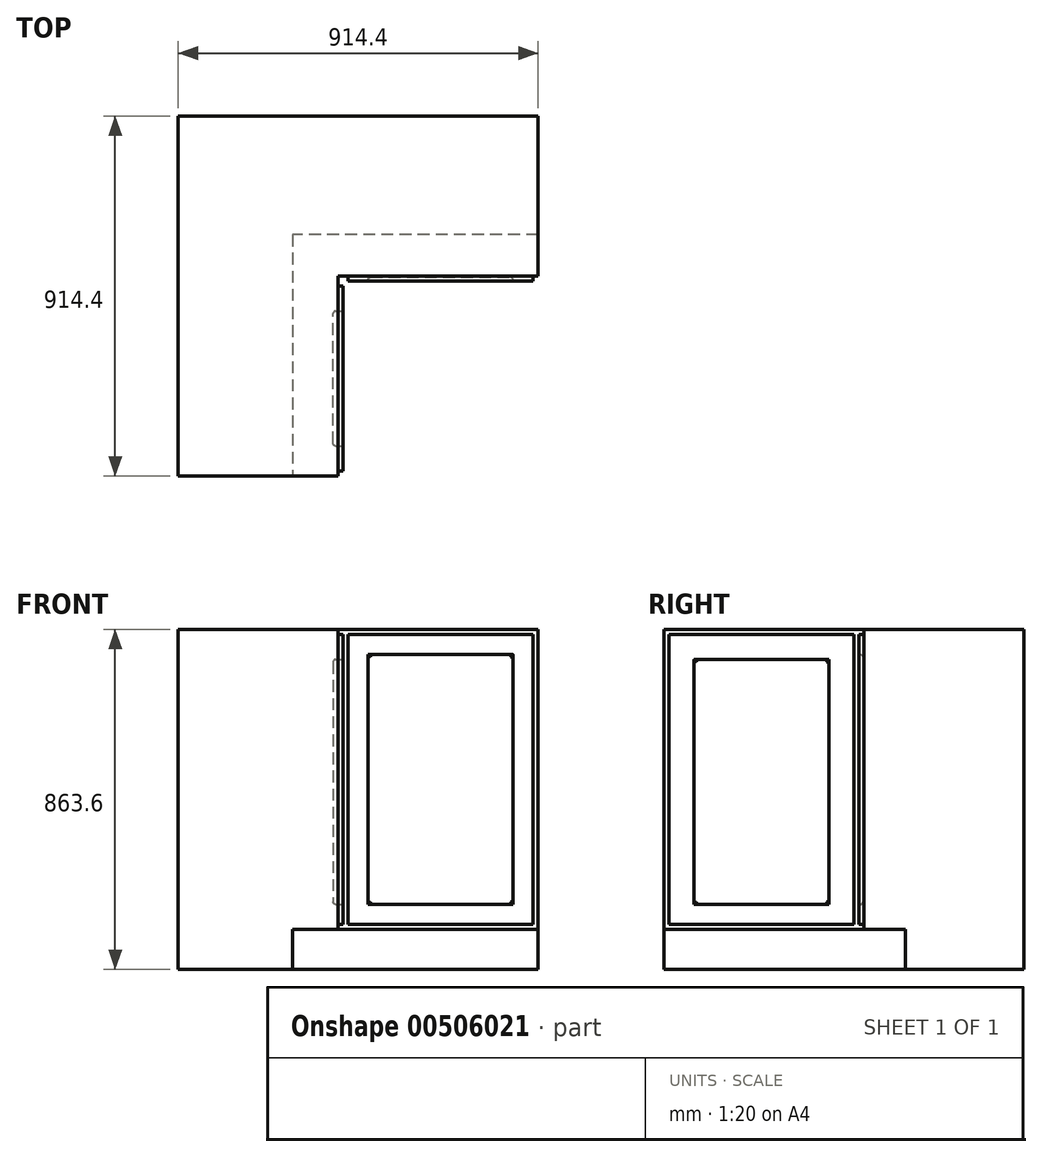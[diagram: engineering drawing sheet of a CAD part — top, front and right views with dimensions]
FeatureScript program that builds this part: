
annotation { "Feature Type Name" : "Feature", "Feature Type Description" : "" }
export const myFeature = defineFeature(function(context is Context, id is Id, definition is map)
    precondition{}
    {
        {
            var Q0;
            Q0=qCreatedBy(makeId("Top.planeOp"),FACE);
            var sketch = newSketch(context, id + "F0", { "sketchPlane" : qUnion([Q0])});
            skLineSegment(sketch, "E0", {"start": v(0, 0) * mm, "end": v(0, 914.4) * mm});
            skLineSegment(sketch, "E1", {"start": v(0, 914.4) * mm, "end": v(914.4, 914.4) * mm});
            skLineSegment(sketch, "E2", {"start": v(914.4, 914.4) * mm, "end": v(914.4, 495.3) * mm});
            skLineSegment(sketch, "E3", {"start": v(914.4, 495.3) * mm, "end": v(419.1, 495.3) * mm});
            skLineSegment(sketch, "E4", {"start": v(419.1, 495.3) * mm, "end": v(419.1, 0) * mm});
            skLineSegment(sketch, "E5", {"start": v(419.1, 0) * mm, "end": v(0, 0) * mm});
            skSolve(sketch);
        }
        {
            var Q0;
            Q0=makeQuery(id+"F0.imprint","IMPRINT",FACE,{"disambiguationData":[TD([[makeQuery(id+"F0.imprint","IMPRINT",EDGE,{"derivedFrom":sQuery(id+"F0.wireOp",EDGE,"E0")}),-1.0]])]});
            extrude(context, id + "F1", {"entities" : qUnion([Q0]), "depth" : 863.6 * mm, "offsetDistance" : 25.4 * mm});
        }
        {
            var Q0;
            Q0=makeQuery(id+"F1.opExtrude","SWEPT_FACE",FACE,{"disambiguationData":[OSD([sQuery(id+"F0.wireOp",EDGE,"E4")])]});
            var sketch = newSketch(context, id + "F2", { "sketchPlane" : qUnion([Q0])});
            skLineSegment(sketch, "E6.bottom", {"start": v(76.2, 787.4) * mm, "end": v(419.1, 787.4) * mm});
            skLineSegment(sketch, "E6.top", {"start": v(76.2, 165.1) * mm, "end": v(419.1, 165.1) * mm});
            skLineSegment(sketch, "E6.left", {"start": v(76.2, 787.4) * mm, "end": v(76.2, 165.1) * mm});
            skLineSegment(sketch, "E6.right", {"start": v(419.1, 787.4) * mm, "end": v(419.1, 165.1) * mm});
            skSolve(sketch);
        }
        {
            var Q0;
            Q0 = qSketchRegion(id + "F2", true);
            extrude(context, id + "F3", {"entities" : qUnion([Q0]), "operationType" : NewBodyOperationType.REMOVE, "oppositeDirection" : true, "depth" : 25.4 * mm, "offsetDistance" : 25.4 * mm});
        }
        {
            var Q0;
            Q0=makeQuery(id+"F3.boolean.opBoolean","COPY",FACE,{"derivedFrom":makeQuery(id+"F3.opExtrude","CAP_FACE",FACE,{"disambiguationData":[OSD([sQuery(id+"F2.wireOp",EDGE,"E6.bottom"),sQuery(id+"F2.wireOp",EDGE,"E6.top"),sQuery(id+"F2.wireOp",EDGE,"E6.left"),sQuery(id+"F2.wireOp",EDGE,"E6.right")])],"isStart":false})});
            var Q1;
            Q1=makeQuery(id+"F3.boolean.opBoolean","COPY",EDGE,{"derivedFrom":makeQuery(id+"F3.opExtrude","CAP_EDGE",EDGE,{"disambiguationData":[OSD([sQuery(id+"F2.wireOp",EDGE,"E6.top")])],"isStart":false})});
            fillet(context, id + "F4", {"entities" : qUnion([Q0, Q1]), "radius" : 6.35 * mm, "tangentPropagation" : true, "allowEdgeOverflow" : false});
        }
        {
            var Q0;
            Q0=makeQuery(id+"F1.opExtrude","SWEPT_FACE",FACE,{"disambiguationData":[OSD([sQuery(id+"F0.wireOp",EDGE,"E3")])]});
            var sketch = newSketch(context, id + "F5", { "sketchPlane" : qUnion([Q0])});
            skLineSegment(sketch, "E7.bottom", {"start": v(482.6, 800.1) * mm, "end": v(850.9, 800.1) * mm});
            skLineSegment(sketch, "E7.top", {"start": v(482.6, 165.1) * mm, "end": v(850.9, 165.1) * mm});
            skLineSegment(sketch, "E7.left", {"start": v(482.6, 800.1) * mm, "end": v(482.6, 165.1) * mm});
            skLineSegment(sketch, "E7.right", {"start": v(850.9, 800.1) * mm, "end": v(850.9, 165.1) * mm});
            skSolve(sketch);
        }
        {
            var Q0;
            Q0 = qSketchRegion(id + "F5", true);
            extrude(context, id + "F6", {"entities" : qUnion([Q0]), "operationType" : NewBodyOperationType.REMOVE, "oppositeDirection" : true, "depth" : 9.65 * mm, "offsetDistance" : 25.4 * mm});
        }
        {
            var Q0;
            Q0=makeQuery(id+"F6.boolean.opBoolean","COPY",FACE,{"derivedFrom":makeQuery(id+"F6.opExtrude","CAP_FACE",FACE,{"disambiguationData":[OSD([sQuery(id+"F5.wireOp",EDGE,"E7.bottom"),sQuery(id+"F5.wireOp",EDGE,"E7.top"),sQuery(id+"F5.wireOp",EDGE,"E7.left"),sQuery(id+"F5.wireOp",EDGE,"E7.right")])],"isStart":false})});
            fillet(context, id + "F7", {"entities" : qUnion([Q0]), "radius" : 6.35 * mm, "tangentPropagation" : true, "allowEdgeOverflow" : false});
        }
        {
            var Q0;
            Q0=makeQuery(id+"F1.opExtrude","CAP_FACE",FACE,{"disambiguationData":[OSD([sQuery(id+"F0.wireOp",EDGE,"E0"),sQuery(id+"F0.wireOp",EDGE,"E1"),sQuery(id+"F0.wireOp",EDGE,"E2"),sQuery(id+"F0.wireOp",EDGE,"E3"),sQuery(id+"F0.wireOp",EDGE,"E4"),sQuery(id+"F0.wireOp",EDGE,"E5")])],"isStart":true});
            var sketch = newSketch(context, id + "F8", { "sketchPlane" : qUnion([Q0])});
            skLineSegment(sketch, "E8", {"start": v(419.1, 0) * mm, "end": v(419.1, -495.3) * mm});
            skLineSegment(sketch, "E9", {"start": v(419.1, -495.3) * mm, "end": v(914.4, -495.3) * mm});
            skLineSegment(sketch, "E10", {"start": v(914.4, -495.3) * mm, "end": v(914.4, -613.26) * mm});
            skLineSegment(sketch, "E11", {"start": v(914.4, -613.26) * mm, "end": v(290.32, -613.26) * mm});
            skLineSegment(sketch, "E12", {"start": v(290.32, -613.26) * mm, "end": v(290.32, 0) * mm});
            skLineSegment(sketch, "E13", {"start": v(290.32, 0) * mm, "end": v(419.1, 0) * mm});
            skSolve(sketch);
        }
        {
            var Q0;
            Q0 = qSketchRegion(id + "F8", true);
            extrude(context, id + "F9", {"entities" : qUnion([Q0]), "operationType" : NewBodyOperationType.REMOVE, "oppositeDirection" : true, "depth" : 101.6 * mm, "offsetDistance" : 25.4 * mm});
        }
        {
            var Q0;
            Q0=makeQuery(id+"F1.opExtrude","SWEPT_FACE",FACE,{"disambiguationData":[OSD([sQuery(id+"F0.wireOp",EDGE,"E4")])]});
            var sketch = newSketch(context, id + "F10", { "sketchPlane" : qUnion([Q0])});
            skLineSegment(sketch, "E14.bottom", {"start": v(0, 863.6) * mm, "end": v(495.3, 863.6) * mm});
            skLineSegment(sketch, "E14.top", {"start": v(0, 101.6) * mm, "end": v(495.3, 101.6) * mm});
            skLineSegment(sketch, "E14.left", {"start": v(0, 863.6) * mm, "end": v(0, 101.6) * mm});
            skLineSegment(sketch, "E14.right", {"start": v(495.3, 863.6) * mm, "end": v(495.3, 101.6) * mm});
            skLineSegment(sketch, "E15.bottom", {"start": v(12.7, 850.9) * mm, "end": v(482.6, 850.9) * mm});
            skLineSegment(sketch, "E15.top", {"start": v(12.7, 114.3) * mm, "end": v(482.6, 114.3) * mm});
            skLineSegment(sketch, "E15.left", {"start": v(12.7, 850.9) * mm, "end": v(12.7, 114.3) * mm});
            skLineSegment(sketch, "E15.right", {"start": v(482.6, 850.9) * mm, "end": v(482.6, 114.3) * mm});
            skSolve(sketch);
        }
        {
            var Q0;
            Q0 = qSketchRegion(id + "F10", true);
            extrude(context, id + "F11", {"entities" : qUnion([Q0]), "operationType" : NewBodyOperationType.REMOVE, "oppositeDirection" : true, "depth" : 12.7 * mm, "offsetDistance" : 25.4 * mm});
        }
        {
            var Q0;
            Q0=makeQuery(id+"F11.boolean.opBoolean","MERGE",FACE,{"derivedFrom":[makeQuery(id+"F1.opExtrude","SWEPT_FACE",FACE,{"disambiguationData":[OSD([sQuery(id+"F0.wireOp",EDGE,"E3")])]}),makeQuery(id+"F11.opExtrude","SWEPT_FACE",FACE,{"disambiguationData":[OSD([sQuery(id+"F10.wireOp",EDGE,"E14.right")])]})]});
            var sketch = newSketch(context, id + "F12", { "sketchPlane" : qUnion([Q0])});
            skLineSegment(sketch, "E16.bottom", {"start": v(406.4, 863.6) * mm, "end": v(914.4, 863.6) * mm});
            skLineSegment(sketch, "E16.top", {"start": v(406.4, 101.6) * mm, "end": v(914.4, 101.6) * mm});
            skLineSegment(sketch, "E16.left", {"start": v(406.4, 863.6) * mm, "end": v(406.4, 101.6) * mm});
            skLineSegment(sketch, "E16.right", {"start": v(914.4, 863.6) * mm, "end": v(914.4, 101.6) * mm});
            skLineSegment(sketch, "E17.bottom", {"start": v(431.8, 850.9) * mm, "end": v(901.7, 850.9) * mm});
            skLineSegment(sketch, "E17.top", {"start": v(431.8, 114.3) * mm, "end": v(901.7, 114.3) * mm});
            skLineSegment(sketch, "E17.left", {"start": v(431.8, 850.9) * mm, "end": v(431.8, 114.3) * mm});
            skLineSegment(sketch, "E17.right", {"start": v(901.7, 850.9) * mm, "end": v(901.7, 114.3) * mm});
            skSolve(sketch);
        }
        {
            var Q0;
            Q0=makeQuery(id+"F12.imprint","IMPRINT",FACE,{"disambiguationData":[TD([[makeQuery(id+"F12.imprint","IMPRINT",EDGE,{"derivedFrom":sQuery(id+"F12.wireOp",EDGE,"E16.bottom")}),1.0]])]});
            extrude(context, id + "F13", {"entities" : qUnion([Q0]), "operationType" : NewBodyOperationType.REMOVE, "oppositeDirection" : true, "depth" : 12.7 * mm, "offsetDistance" : 25.4 * mm});
        }
    });
